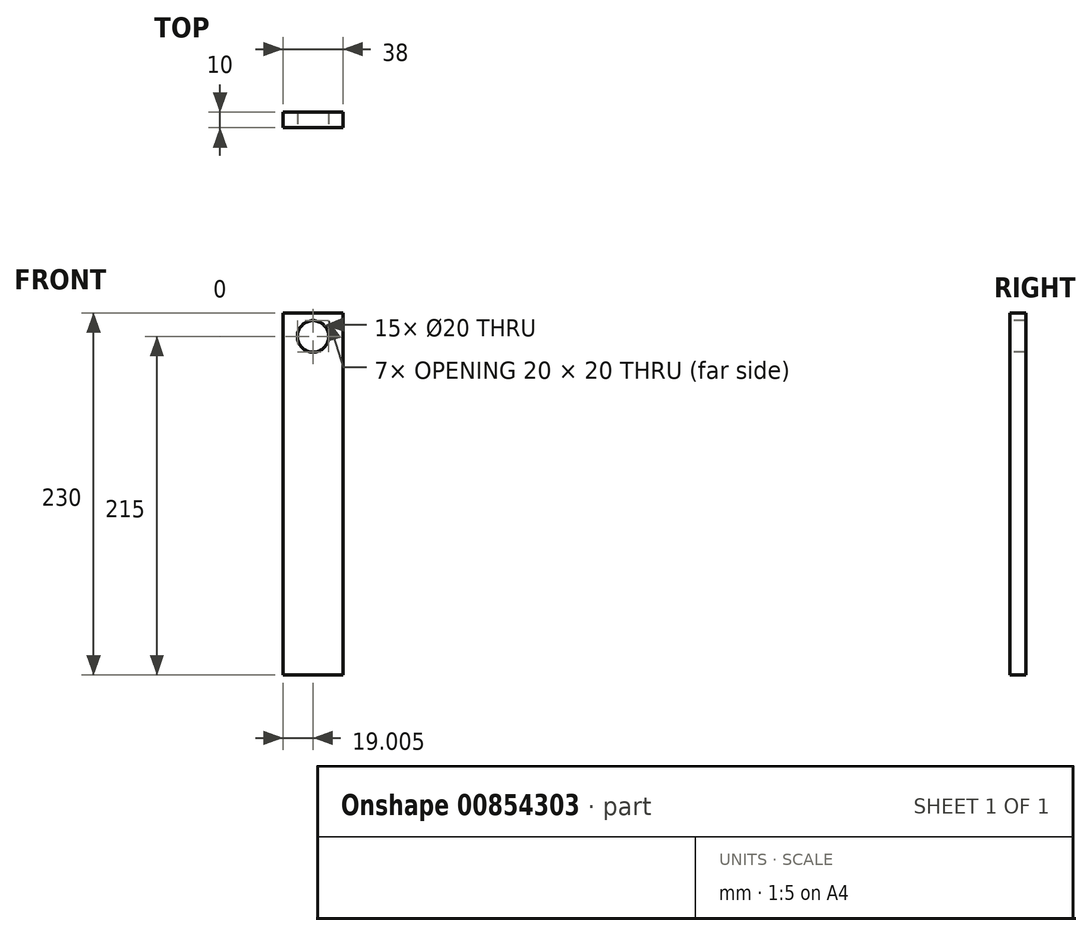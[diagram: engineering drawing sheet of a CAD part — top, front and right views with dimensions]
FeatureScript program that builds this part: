
annotation { "Feature Type Name" : "Feature", "Feature Type Description" : "" }
export const myFeature = defineFeature(function(context is Context, id is Id, definition is map)
    precondition{}
    {
        {
            var Q0;
            Q0=qCreatedBy(makeId("Top.planeOp"),FACE);
            var sketch = newSketch(context, id + "F0", { "sketchPlane" : qUnion([Q0])});
            skLineSegment(sketch, "E0.bottom", {"start": v(-22, -3.17) * mm, "end": v(16, -3.17) * mm});
            skLineSegment(sketch, "E0.top", {"start": v(-22, -13.17) * mm, "end": v(16, -13.17) * mm});
            skLineSegment(sketch, "E0.left", {"start": v(-22, -3.17) * mm, "end": v(-22, -13.17) * mm});
            skLineSegment(sketch, "E0.right", {"start": v(16, -3.17) * mm, "end": v(16, -13.17) * mm});
            skSolve(sketch);
        }
        {
            var Q0;
            Q0=makeQuery(id+"F0.imprint","IMPRINT",FACE,{"disambiguationData":[TD([[makeQuery(id+"F0.imprint","IMPRINT",EDGE,{"derivedFrom":sQuery(id+"F0.wireOp",EDGE,"E0.bottom")}),-1.0]])]});
            extrude(context, id + "F1", {"entities" : qUnion([Q0]), "depth" : 230 * mm, "offsetDistance" : 25 * mm});
        }
        {
            var Q0;
            Q0=makeQuery(id+"F1.opExtrude","SWEPT_FACE",FACE,{"disambiguationData":[OSD([sQuery(id+"F0.wireOp",EDGE,"E0.top")])]});
            var sketch = newSketch(context, id + "F2", { "sketchPlane" : qUnion([Q0])});
            skCircle(sketch, "E1", {"center": v(-3, 215) * mm, "radius": 10 * mm});
            skSolve(sketch);
        }
        {
            var Q0;
            Q0=makeQuery(id+"F2.imprint","IMPRINT",FACE,{"disambiguationData":[TD([[makeQuery(id+"F2.imprint","IMPRINT",EDGE,{"derivedFrom":sQuery(id+"F2.wireOp",EDGE,"E1")}),1.0]])]});
            extrude(context, id + "F3", {"entities" : qUnion([Q0]), "operationType" : NewBodyOperationType.REMOVE, "oppositeDirection" : true, "depth" : 25 * mm, "offsetDistance" : 25 * mm});
        }
    });
